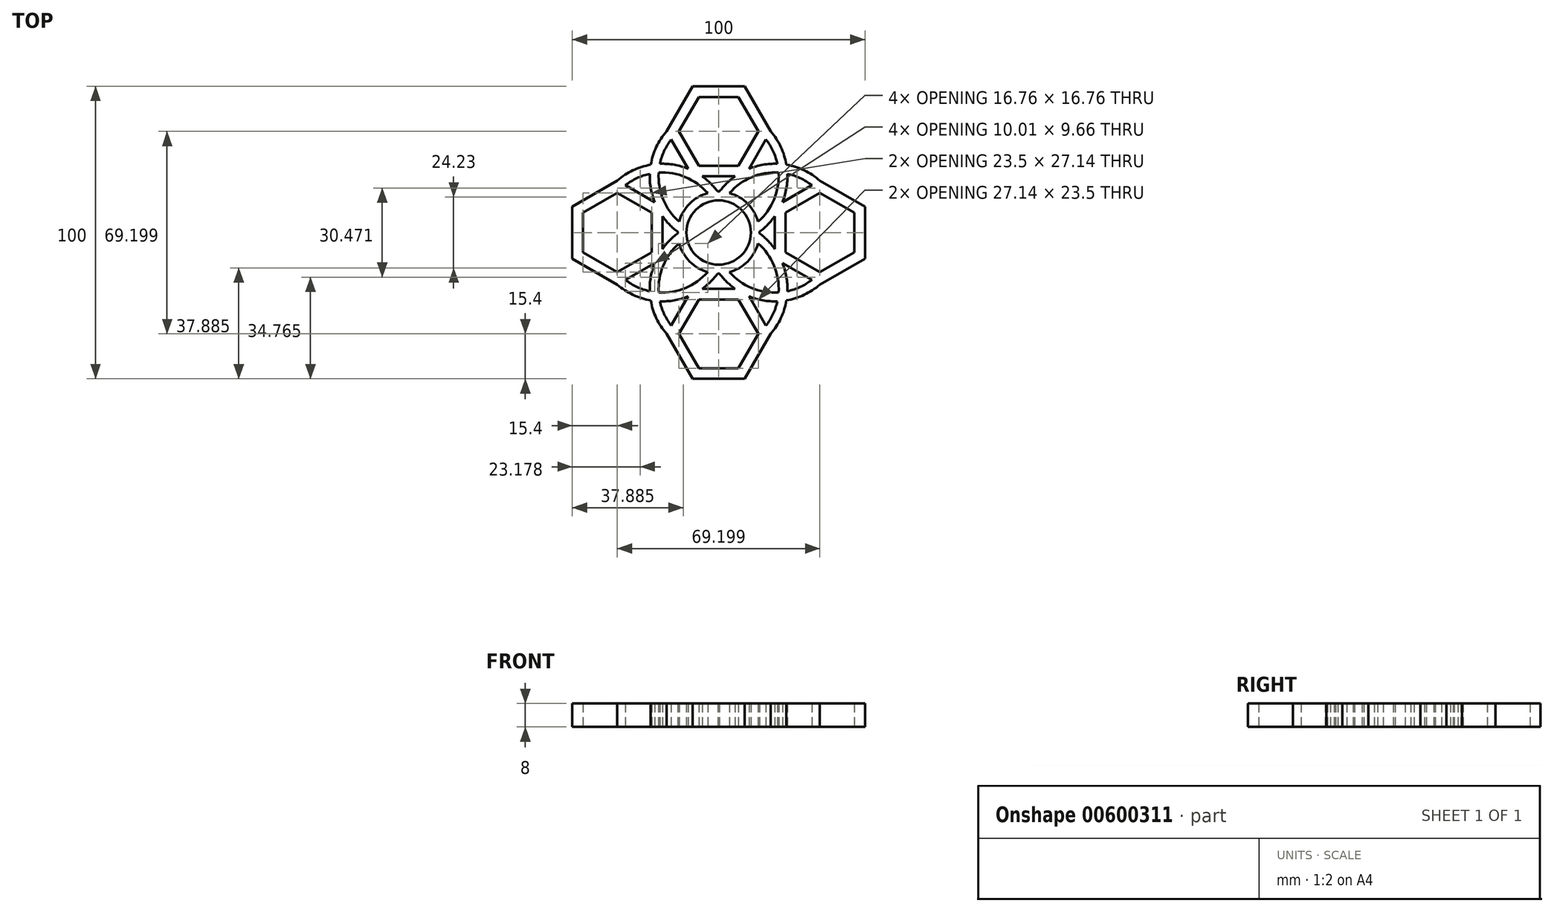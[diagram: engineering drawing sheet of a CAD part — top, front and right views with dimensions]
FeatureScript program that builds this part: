
annotation { "Feature Type Name" : "Feature", "Feature Type Description" : "" }
export const myFeature = defineFeature(function(context is Context, id is Id, definition is map)
    precondition{}
    {
        {
            var Q0;
            Q0=qCreatedBy(makeId("Top.planeOp"),FACE);
            var sketch = newSketch(context, id + "F0", { "sketchPlane" : qUnion([Q0])});
            skLineSegment(sketch, "E0", {"start": v(0, 34.6) * mm, "end": v(0, 0) * mm, "construction": true});
            skLineSegment(sketch, "E1", {"start": v(0, 0) * mm, "end": v(-29.96, -17.3) * mm, "construction": true});
            skLineSegment(sketch, "E2", {"start": v(0, 0) * mm, "end": v(29.96, -17.3) * mm, "construction": true});
            skArc(sketch, "E3", {"start": v(-14, 0.3) * mm, "mid": v(0, -14) * mm, "end": v(14, 0.3) * mm});
            skCircle(sketch, "E4.cCircle", {"center": v(0, 34.6) * mm, "radius": 11.75 * mm, "construction": true});
            skLineSegment(sketch, "E4.0", {"start": v(13.57, 34.6) * mm, "end": v(6.78, 22.85) * mm});
            skLineSegment(sketch, "E4.1", {"start": v(6.78, 22.85) * mm, "end": v(-6.78, 22.85) * mm});
            skLineSegment(sketch, "E4.2", {"start": v(-6.78, 22.85) * mm, "end": v(-13.57, 34.6) * mm});
            skLineSegment(sketch, "E4.3", {"start": v(-13.57, 34.6) * mm, "end": v(-6.78, 46.35) * mm});
            skLineSegment(sketch, "E4.4", {"start": v(-6.78, 46.35) * mm, "end": v(6.78, 46.35) * mm});
            skLineSegment(sketch, "E4.5", {"start": v(6.78, 46.35) * mm, "end": v(13.57, 34.6) * mm});
            skPoint(sketch, "E4.0.midPoint", {"position": v(10.18, 28.72) * mm});
            skCircle(sketch, "E5.cCircle", {"center": v(0, 34.6) * mm, "radius": 15.4 * mm, "construction": true});
            skLineSegment(sketch, "E5.0", {"start": v(16.18, 31.83) * mm, "end": v(8.9, 19.2) * mm});
            skLineSegment(sketch, "E5.1", {"start": v(8.9, 19.2) * mm, "end": v(-8.9, 19.2) * mm});
            skLineSegment(sketch, "E5.2", {"start": v(-8.9, 19.2) * mm, "end": v(-16.18, 31.83) * mm});
            skLineSegment(sketch, "E5.3", {"start": v(-17.78, 34.6) * mm, "end": v(-8.9, 50) * mm});
            skLineSegment(sketch, "E5.4", {"start": v(-8.9, 50) * mm, "end": v(8.9, 50) * mm});
            skLineSegment(sketch, "E5.5", {"start": v(8.9, 50) * mm, "end": v(17.78, 34.6) * mm});
            skPoint(sketch, "E5.0.midPoint", {"position": v(13.34, 26.9) * mm});
            skLineSegment(sketch, "E6.1", {"start": v(-16.18, 31.83) * mm, "end": v(-8.9, 19.2) * mm});
            skLineSegment(sketch, "E7.0", {"start": v(8.9, 19.2) * mm, "end": v(16.18, 31.83) * mm});
            skPoint(sketch, "E7.0.midPoint", {"position": v(14.07, 28.17) * mm});
            skArc(sketch, "E8", {"start": v(-17.78, 34.6) * mm, "mid": v(-23.38, 16.62) * mm, "end": v(-14, 0.3) * mm});
            skArc(sketch, "E9", {"start": v(-16.18, 31.83) * mm, "mid": v(-20.43, 17.24) * mm, "end": v(-13.5, 3.73) * mm});
            skArc(sketch, "E10.trimOffspring", {"start": v(-10.23, 40.38) * mm, "mid": v(-10.23, 40.38) * mm, "end": v(-10.23, 40.38) * mm});
            skArc(sketch, "E11.trimOffspring", {"start": v(10.23, 40.38) * mm, "mid": v(10.23, 40.38) * mm, "end": v(10.23, 40.38) * mm});
            skArc(sketch, "E12.trimOffspring", {"start": v(13.5, 3.73) * mm, "mid": v(20.43, 17.24) * mm, "end": v(16.18, 31.83) * mm});
            skArc(sketch, "E13.trimOffspring", {"start": v(14, 0.3) * mm, "mid": v(23.38, 16.62) * mm, "end": v(17.78, 34.6) * mm});
            skArc(sketch, "E14.trimOffspring", {"start": v(13.5, 3.73) * mm, "mid": v(0, 14) * mm, "end": v(-13.5, 3.73) * mm});
            skCircle(sketch, "E15", {"center": v(0, 0) * mm, "radius": 11 * mm});
            skSolve(sketch);
        }
        {
            var Q0;
            Q0 = qSketchRegion(id + "F0", true);
            extrude(context, id + "F1", {"entities" : qUnion([Q0]), "endBound" : BoundingType.SYMMETRIC, "depth" : 8 * mm, "offsetDistance" : 25 * mm});
        }
        {
            var Q0;
            Q0=makeQuery(id+"F1.opExtrude","SWEPT_BODY",BODY,{"disambiguationData":[OSD([sQuery(id+"F0.wireOp",EDGE,"E3"),sQuery(id+"F0.wireOp",EDGE,"E4.0"),sQuery(id+"F0.wireOp",EDGE,"E4.1"),sQuery(id+"F0.wireOp",EDGE,"E4.2"),sQuery(id+"F0.wireOp",EDGE,"E4.3"),sQuery(id+"F0.wireOp",EDGE,"E4.4"),sQuery(id+"F0.wireOp",EDGE,"E4.5"),sQuery(id+"F0.wireOp",EDGE,"E5.1"),sQuery(id+"F0.wireOp",EDGE,"E5.3"),sQuery(id+"F0.wireOp",EDGE,"E5.4"),sQuery(id+"F0.wireOp",EDGE,"E5.5"),sQuery(id+"F0.wireOp",EDGE,"E6.1"),sQuery(id+"F0.wireOp",EDGE,"E7.0"),sQuery(id+"F0.wireOp",EDGE,"E8"),sQuery(id+"F0.wireOp",EDGE,"E9"),sQuery(id+"F0.wireOp",EDGE,"E12.trimOffspring"),sQuery(id+"F0.wireOp",EDGE,"E13.trimOffspring"),sQuery(id+"F0.wireOp",EDGE,"E14.trimOffspring"),sQuery(id+"F0.wireOp",EDGE,"E15")])]});
            var Q1;
            Q1=makeQuery(id+"F1.opExtrude","CAP_EDGE",EDGE,{"disambiguationData":[OSD([sQuery(id+"F0.wireOp",EDGE,"E15")])],"isStart":false});
            circularPattern(context, id + "F2", {"operationType" : NewBodyOperationType.ADD, "entities" : qUnion([Q0]), "axis" : qUnion([Q1]), "angle" : 360 * degree, "instanceCount" : 4, "equalSpace" : true});
        }
    });
